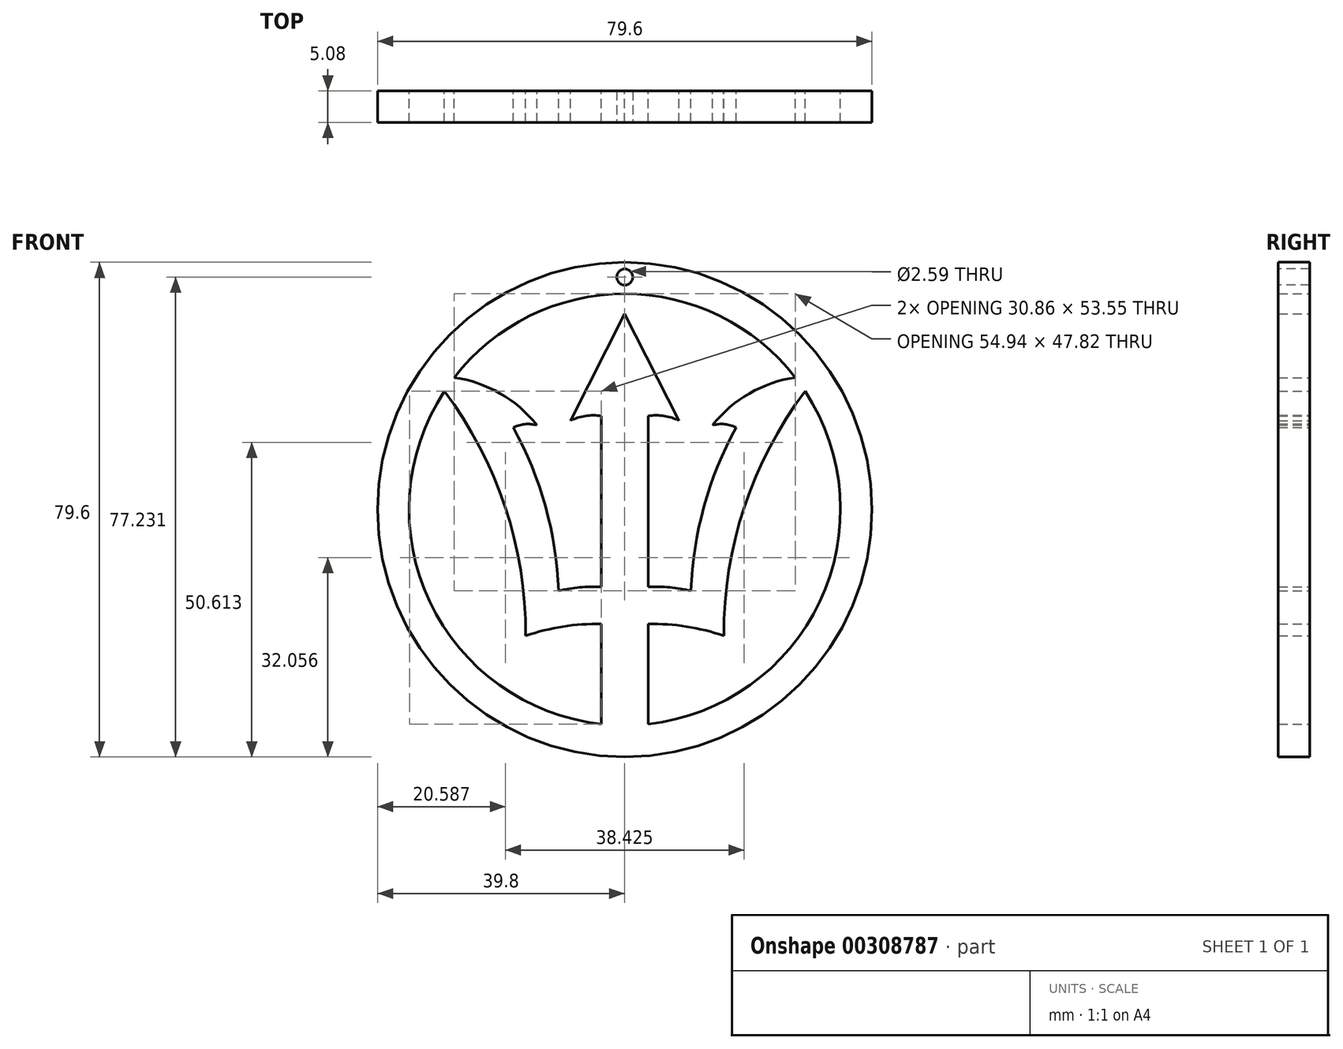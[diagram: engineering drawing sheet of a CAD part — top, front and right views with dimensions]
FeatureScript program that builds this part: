
annotation { "Feature Type Name" : "Feature", "Feature Type Description" : "" }
export const myFeature = defineFeature(function(context is Context, id is Id, definition is map)
    precondition{}
    {
        {
            var Q0;
            Q0=qCreatedBy(makeId("Front.planeOp"),FACE);
            var sketch = newSketch(context, id + "F0", { "sketchPlane" : qUnion([Q0])});
            skArc(sketch, "E0", {"start": v(-15.94, -20.31) * mm, "mid": v(-19.76, 1.89) * mm, "end": v(-30.96, 21.43) * mm});
            skArc(sketch, "E1", {"start": v(-14.15, 13.58) * mm, "mid": v(-21.62, 19.5) * mm, "end": v(-30.96, 21.43) * mm});
            skArc(sketch, "E2", {"start": v(-14.15, 13.58) * mm, "mid": v(-16.09, 13.74) * mm, "end": v(-17.96, 13.2) * mm});
            skArc(sketch, "E3", {"start": v(-10.65, -13.1) * mm, "mid": v(-12.76, 0.48) * mm, "end": v(-17.96, 13.2) * mm});
            skArc(sketch, "E4", {"start": v(-3.8, -12.46) * mm, "mid": v(-7.25, -12.53) * mm, "end": v(-10.65, -13.1) * mm});
            skLineSegment(sketch, "E5", {"start": v(-3.8, -12.46) * mm, "end": v(-3.8, 15.08) * mm});
            skArc(sketch, "E6", {"start": v(-3.8, 15.08) * mm, "mid": v(-6.33, 15.08) * mm, "end": v(-8.75, 14.32) * mm});
            skLineSegment(sketch, "E7", {"start": v(-8.75, 14.32) * mm, "end": v(0, 31.52) * mm});
            skArc(sketch, "E8", {"start": v(-3.79, -18.4) * mm, "mid": v(-9.94, -18.83) * mm, "end": v(-15.94, -20.31) * mm});
            skLineSegment(sketch, "E9", {"start": v(-3.79, -18.4) * mm, "end": v(-3.79, -34.78) * mm});
            skLineSegment(sketch, "E10", {"start": v(-3.79, -34.78) * mm, "end": v(0, -34.78) * mm});
            skLineSegment(sketch, "E11", {"start": v(0, 31.52) * mm, "end": v(0, -34.78) * mm});
            skLineSegment(sketch, "E12.MirrorCS", {"start": v(3.78, -34.78) * mm, "end": v(0, -34.78) * mm});
            skLineSegment(sketch, "E13.MirrorCS", {"start": v(3.78, -18.4) * mm, "end": v(3.78, -34.78) * mm});
            skArc(sketch, "E14.MirrorCS", {"start": v(3.78, -18.4) * mm, "mid": v(9.94, -18.83) * mm, "end": v(15.94, -20.31) * mm});
            skArc(sketch, "E15.MirrorCS", {"start": v(15.94, -20.31) * mm, "mid": v(19.75, 1.89) * mm, "end": v(30.96, 21.43) * mm});
            skArc(sketch, "E16.MirrorCS", {"start": v(14.15, 13.58) * mm, "mid": v(21.62, 19.5) * mm, "end": v(30.96, 21.43) * mm});
            skArc(sketch, "E17.MirrorCS", {"start": v(10.65, -13.1) * mm, "mid": v(12.76, 0.48) * mm, "end": v(17.96, 13.2) * mm});
            skArc(sketch, "E18.MirrorCS", {"start": v(3.8, -12.46) * mm, "mid": v(7.25, -12.53) * mm, "end": v(10.65, -13.1) * mm});
            skLineSegment(sketch, "E19.MirrorCS", {"start": v(3.8, -12.46) * mm, "end": v(3.8, 15.08) * mm});
            skArc(sketch, "E20.MirrorCS", {"start": v(3.8, 15.08) * mm, "mid": v(6.33, 15.08) * mm, "end": v(8.75, 14.32) * mm});
            skLineSegment(sketch, "E21.MirrorCS", {"start": v(8.75, 14.32) * mm, "end": v(0, 31.52) * mm});
            skSolve(sketch);
        }
        {
            var Q0;
            Q0=makeQuery(id+"F0.imprint","IMPRINT",FACE,{"disambiguationData":[TD([[makeQuery(id+"F0.imprint","IMPRINT",EDGE,{"derivedFrom":sQuery(id+"F0.wireOp",EDGE,"E0")}),-1.0]])]});
            extrude(context, id + "F1", {"entities" : qUnion([Q0]), "depth" : 5.08 * mm});
        }
        {
            var Q0;
            Q0=makeQuery(id+"F1.opExtrude","SWEPT_BODY",BODY,{"disambiguationData":[OSD([sQuery(id+"F0.wireOp",EDGE,"E0"),sQuery(id+"F0.wireOp",EDGE,"E1"),sQuery(id+"F0.wireOp",EDGE,"E2"),sQuery(id+"F0.wireOp",EDGE,"E3"),sQuery(id+"F0.wireOp",EDGE,"E4"),sQuery(id+"F0.wireOp",EDGE,"E5"),sQuery(id+"F0.wireOp",EDGE,"E6"),sQuery(id+"F0.wireOp",EDGE,"E7"),sQuery(id+"F0.wireOp",EDGE,"E8"),sQuery(id+"F0.wireOp",EDGE,"E9"),sQuery(id+"F0.wireOp",EDGE,"E10"),sQuery(id+"F0.wireOp",EDGE,"E11")])]});
            var Q1;
            Q1=qCreatedBy(makeId("Right.planeOp"),FACE);
            mirror(context, id + "F2", {"operationType" : NewBodyOperationType.ADD, "entities" : qUnion([Q0]), "mirrorPlane" : qUnion([Q1])});
        }
        {
            var Q0;
            Q0=qCreatedBy(makeId("Front.planeOp"),FACE);
            var sketch = newSketch(context, id + "F3", { "sketchPlane" : qUnion([Q0])});
            skCircle(sketch, "E22", {"center": v(0, 0) * mm, "radius": 34.72 * mm});
            skCircle(sketch, "E23.0", {"center": v(0, 0) * mm, "radius": 39.8 * mm});
            skSolve(sketch);
        }
        {
            var Q0;
            Q0=makeQuery(id+"F3.imprint","IMPRINT",FACE,{"disambiguationData":[TD([[makeQuery(id+"F3.imprint","IMPRINT",EDGE,{"derivedFrom":sQuery(id+"F3.wireOp",EDGE,"E22")}),-1.0]])]});
            extrude(context, id + "F4", {"entities" : qUnion([Q0]), "operationType" : NewBodyOperationType.ADD, "depth" : 5.08 * mm});
        }
        {
            var Q0;
            {var subQ0=makeQuery(id+"F1.opExtrude","CAP_FACE",FACE,{"disambiguationData":[OSD([sQuery(id+"F0.wireOp",EDGE,"E0"),sQuery(id+"F0.wireOp",EDGE,"E1"),sQuery(id+"F0.wireOp",EDGE,"E2"),sQuery(id+"F0.wireOp",EDGE,"E3"),sQuery(id+"F0.wireOp",EDGE,"E4"),sQuery(id+"F0.wireOp",EDGE,"E5"),sQuery(id+"F0.wireOp",EDGE,"E6"),sQuery(id+"F0.wireOp",EDGE,"E7"),sQuery(id+"F0.wireOp",EDGE,"E8"),sQuery(id+"F0.wireOp",EDGE,"E9"),sQuery(id+"F0.wireOp",EDGE,"E10"),sQuery(id+"F0.wireOp",EDGE,"E11")])],"isStart":false});Q0=makeQuery(id+"F4.boolean.opBoolean","MERGE",FACE,{"derivedFrom":[makeQuery(id+"F2.boolean.opBoolean","MERGE",FACE,{"derivedFrom":[subQ0,makeQuery(id+"F2.opPattern","COPY",FACE,{"derivedFrom":subQ0,"instanceName":"1"})]}),makeQuery(id+"F4.opExtrude","CAP_FACE",FACE,{"disambiguationData":[OSD([sQuery(id+"F3.wireOp",EDGE,"E22"),sQuery(id+"F3.wireOp",EDGE,"E23.0")])],"isStart":false})]});}
            var sketch = newSketch(context, id + "F5", { "sketchPlane" : qUnion([Q0])});
            skCircle(sketch, "E24", {"center": v(0, 37.43) * mm, "radius": 1.3 * mm});
            skPoint(sketch, "E24.centerSnap0", {"position": v(0, 34.72) * mm});
            skSolve(sketch);
        }
        {
            var Q0;
            Q0=makeQuery(id+"F5.imprint","IMPRINT",FACE,{"disambiguationData":[TD([[makeQuery(id+"F5.imprint","IMPRINT",EDGE,{"derivedFrom":sQuery(id+"F5.wireOp",EDGE,"E24")}),1.0]])]});
            extrude(context, id + "F6", {"entities" : qUnion([Q0]), "operationType" : NewBodyOperationType.REMOVE, "oppositeDirection" : true, "depth" : 25.4 * mm});
        }
    });
